# Revit family: Multisensor For Roomset _331X
name_source: partatom
category: Electrical Fixtures
revit_build: Autodesk Revit 2018 (Build: 20170223_1515(x64)
units: mm (PartAtom-declared; Revit-internal decimal feet)

## family parameters
Always vertical = Yes
Cut with Voids When Loaded = No
Maintain Annotation Orientation = No
Part Type = Normal
Room Calculation Point = No
Round Connector Dimension = Use Diameter
Shared = No
Work Plane-Based = Yes

## types (1)
- Multisensor For Roomset_Black/White
    Ambient temperature = 0 °C to +50 °C
    Bezel diameter = 66 mm
    Bluetooth®: = BLE 4.1
    Cable rating = All cables must be mains rated.
    DALI : = Removable connector block
    DALI consumption: = 40 mA
    DALI standard = IEC 62386
    DALI supply input = 9.5 V – 22.5 V
    Default Elevation = 0 mm  [stored 0 ft]
    EMC emission = EN 61000-6-3
    EMC immunity = EN 61547
    Environment = Complies with WEEE and RoHS directives.
    Finish / Colour: = 331  Semi-matt / White RAL 9003
331B Semi-matt / Anthracite grey RAL 7016
    IP code: = IP30 [IP20 cable cover]
    Light sensor = For constant-light functions
    Manufacturer = Helvar
    Material (casing): = Nonflammable PC/ABS (UL94–V0)
    Max. recommended mounting height = 4 m
    Model = 331/331B
    Mounting hole diameter: = 52 mm – 55 mm
    Presence detection coverage area = 46 m² @ 2.5 m mounting height
    Presence detector = Passive infrared (PIR)
    RED = EN 300328, EN 301489-17
    Recommended clearance depth = 10 cm (with cable cover, incl. 5 cm
for cabling)
    Relative humidity = Max. 90 %, noncondensing
    SPRING ANGLE = 30.00°
    Safety = EN 61347-2-11
    Software = Android 6.0.2 or later BLE 4.1 or later
    Storage temperature = −10 °C to +70 °C
    Tablet = Tablet (9.7˝ screen or larger recommended)
    Weight = 56 g
    Wire section = 0.5 mm² – 1.5 mm² solid or stranded

note: [stored X ft] marks values corroborated as IEEE doubles in the binary element streams (Revit-internal decimal feet)

## geometry (parser evidence)
native form markers: Sweep x10
no freeform markers — native parametric forms only
